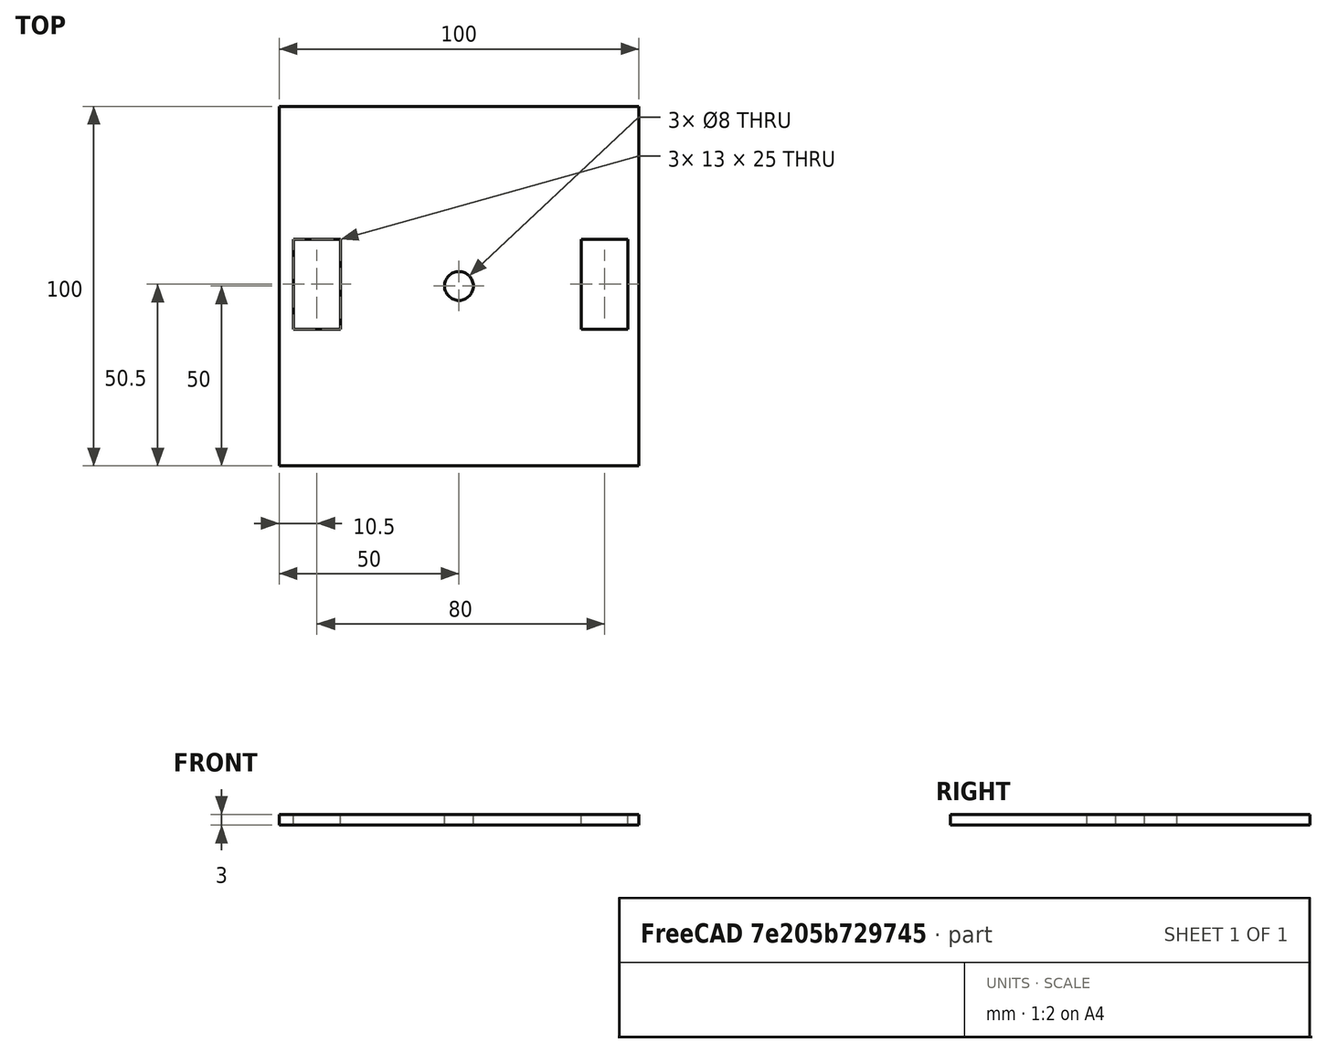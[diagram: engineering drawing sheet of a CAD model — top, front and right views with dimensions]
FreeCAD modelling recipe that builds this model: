
FCSTD DOCUMENT  (FreeCAD 0.16R6707 (Git))
Label: turretBasementTop
License: All rights reserved
LicenseURL: http://en.wikipedia.org/wiki/All_rights_reserved
objects: Part::Box×3, Part::Cut×3, Part::Cylinder×1, Part::Part2DObjectPython×1
note: 8 computed .brp shape members not serialized (recipe doc carries the construction recipe); baked Part::Feature solids carry a one-line shape summary decoded from their .brp

FEATURE [Part::Box] Box  label="Cube"
  Height = 3
  Length = 100
  Placement = pos=(-50,-50,0) rot=(0,0,1;0rad)
  Width = 100
FEATURE [Part::Cylinder] Cylinder
  Angle = 360
  Height = 3
  Radius = 4
FEATURE [Part::Cut] Cut
  Base = -> Box
  Tool = -> Cylinder
FEATURE [Part::Box] Box001  label="Cube001"
  Height = 3
  Length = 13
  Placement = pos=(34,-12,0) rot=(0,0,1;0rad)
  Width = 25
FEATURE [Part::Cut] Cut001
  Base = -> Cut
  Tool = -> Box001
FEATURE [Part::Box] Box002  label="Cube002"
  Height = 3
  Length = 13
  Placement = pos=(-46,-12,0) rot=(0,0,1;0rad)
  Width = 25
FEATURE [Part::Cut] Cut002
  Base = -> Cut001
  Tool = -> Box002
FEATURE [Part::Part2DObjectPython] Shape2DView  # Draft 2D object (typed FeaturePython)
  Base = -> Cut002
  FaceNumbers = [2]
  HiddenLines = false
  Projection = (0,0,1)
  ProjectionMode = 0
  SegmentLength = 0.05
  Tessellation = false
